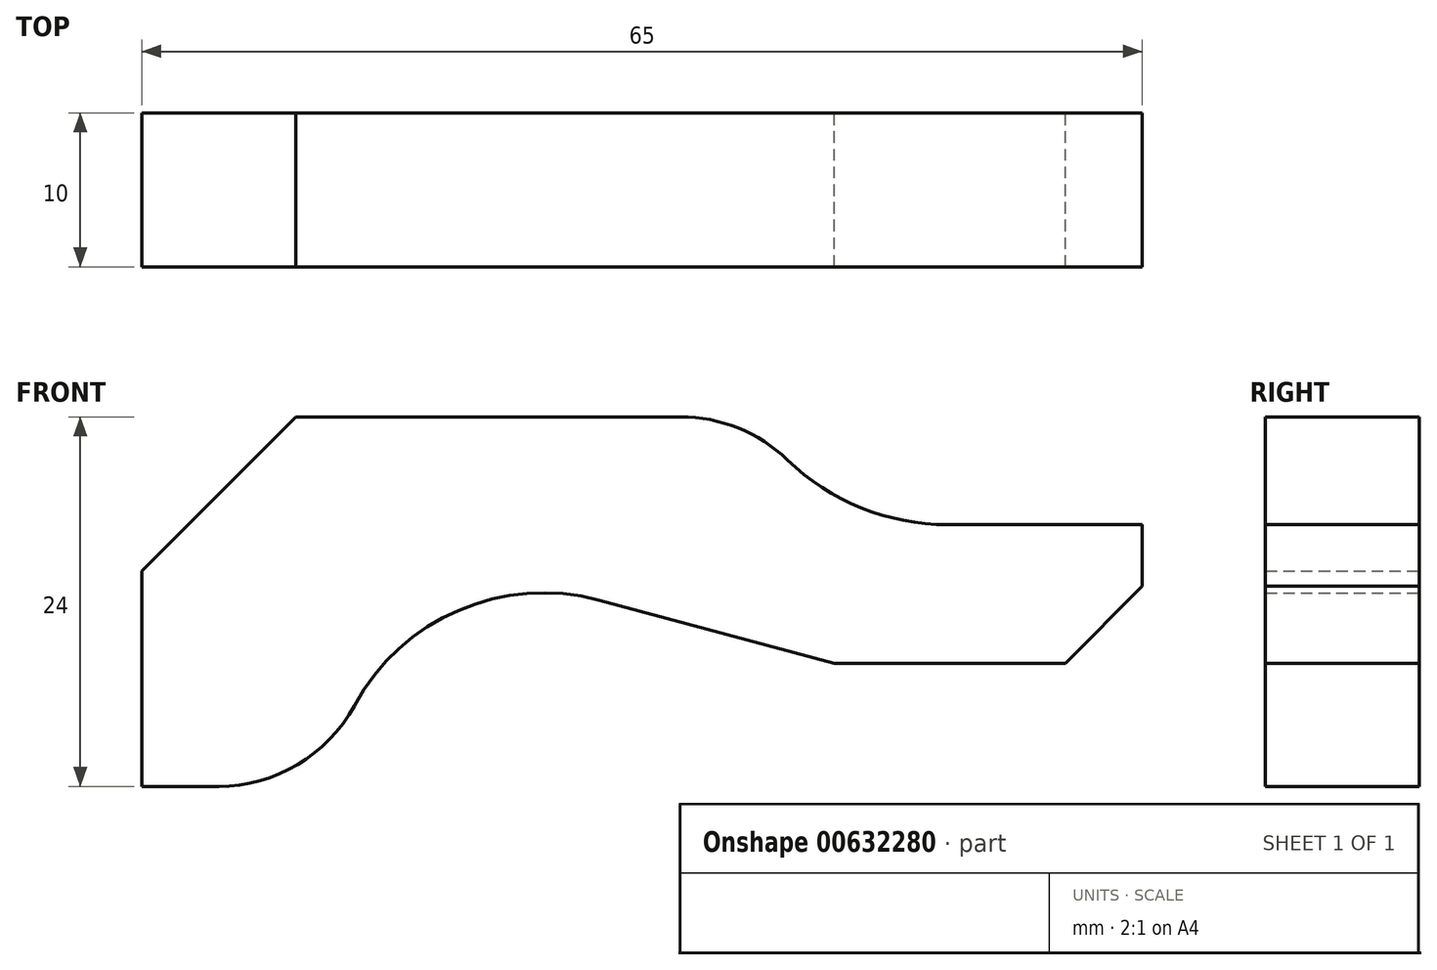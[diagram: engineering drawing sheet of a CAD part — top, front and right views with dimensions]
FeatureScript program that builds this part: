
annotation { "Feature Type Name" : "Feature", "Feature Type Description" : "" }
export const myFeature = defineFeature(function(context is Context, id is Id, definition is map)
    precondition{}
    {
        {
            var Q0;
            Q0=qCreatedBy(makeId("Front.planeOp"),FACE);
            var sketch = newSketch(context, id + "F0", { "sketchPlane" : qUnion([Q0])});
            skLineSegment(sketch, "E0", {"start": v(0, 0) * mm, "end": v(0, 14) * mm});
            skLineSegment(sketch, "E1", {"start": v(0, 14) * mm, "end": v(10, 24) * mm});
            skLineSegment(sketch, "E2", {"start": v(10, 24) * mm, "end": v(35, 24) * mm});
            skLineSegment(sketch, "E3", {"start": v(0, 0) * mm, "end": v(5, 0) * mm});
            skArc(sketch, "E4", {"start": v(13.8, 5.24) * mm, "mid": v(10.12, 1.4) * mm, "end": v(5, 0) * mm});
            skPoint(sketch, "E4.centerSnap0", {"position": v(-2.15, 10) * mm});
            skArc(sketch, "E5", {"start": v(13.8, 5.24) * mm, "mid": v(20.57, 11.43) * mm, "end": v(29.73, 12.1) * mm});
            skArc(sketch, "E6", {"start": v(35, 24) * mm, "mid": v(38.74, 23.27) * mm, "end": v(41.94, 21.2) * mm});
            skArc(sketch, "E7", {"start": v(41.94, 21.2) * mm, "mid": v(46.74, 18.09) * mm, "end": v(52.35, 17) * mm});
            skLineSegment(sketch, "E8", {"start": v(52.35, 17) * mm, "end": v(65, 17) * mm});
            skLineSegment(sketch, "E9", {"start": v(65, 17) * mm, "end": v(65, 13) * mm});
            skLineSegment(sketch, "E10", {"start": v(65, 13) * mm, "end": v(60, 8) * mm});
            skLineSegment(sketch, "E11", {"start": v(60, 8) * mm, "end": v(45, 8) * mm});
            skLineSegment(sketch, "E12", {"start": v(45, 8) * mm, "end": v(29.73, 12.1) * mm});
            skSolve(sketch);
        }
        {
            var Q0;
            Q0 = qSketchRegion(id + "F0", true);
            extrude(context, id + "F1", {"entities" : qUnion([Q0]), "depth" : 10 * mm, "offsetDistance" : 25 * mm});
        }
    });
